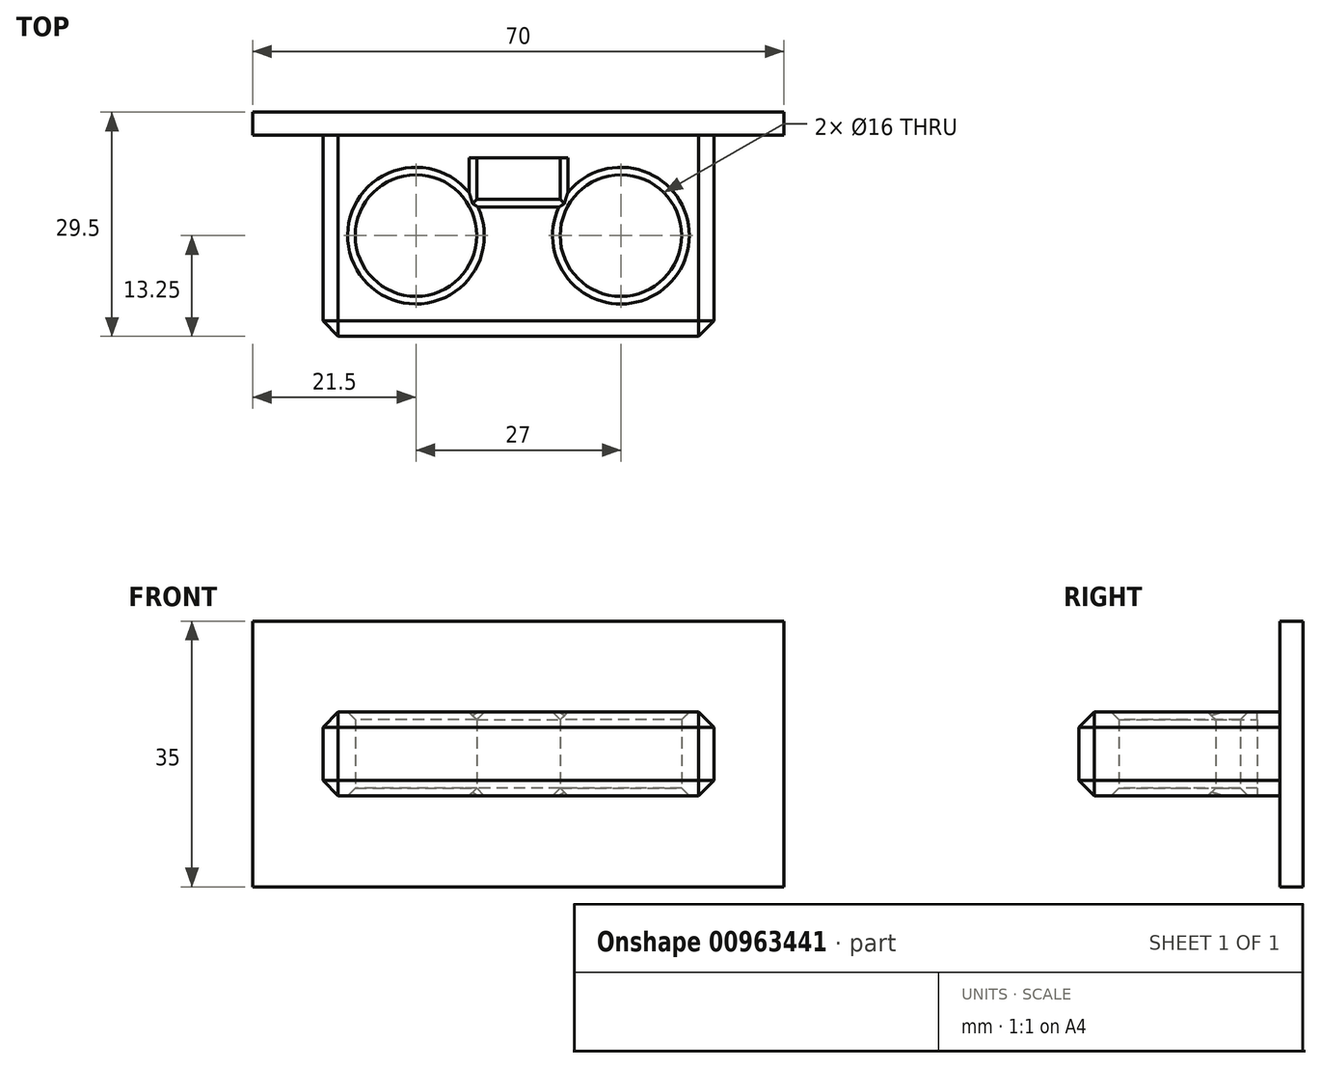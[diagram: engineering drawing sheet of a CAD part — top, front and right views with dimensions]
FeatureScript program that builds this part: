
annotation { "Feature Type Name" : "Feature", "Feature Type Description" : "" }
export const myFeature = defineFeature(function(context is Context, id is Id, definition is map)
    precondition{}
    {
        {
            var Q0;
            Q0=qCreatedBy(makeId("Top.planeOp"),FACE);
            var sketch = newSketch(context, id + "F0", { "sketchPlane" : qUnion([Q0])});
            skLineSegment(sketch, "E0.bottom", {"start": v(22.75, 10.25) * mm, "end": v(-22.75, 10.25) * mm});
            skLineSegment(sketch, "E0.top", {"start": v(22.75, -10.25) * mm, "end": v(-22.75, -10.25) * mm});
            skLineSegment(sketch, "E0.left", {"start": v(22.75, 10.25) * mm, "end": v(22.75, -10.25) * mm});
            skLineSegment(sketch, "E0.right", {"start": v(-22.75, 10.25) * mm, "end": v(-22.75, -10.25) * mm});
            skPoint(sketch, "E0.middle", {"position": v(0, 0) * mm});
            skLineSegment(sketch, "E1.bottom", {"start": v(13.5, 0) * mm, "end": v(-13.5, 0) * mm});
            skLineSegment(sketch, "E1.top", {"start": v(13.5, 0) * mm, "end": v(-13.5, 0) * mm});
            skLineSegment(sketch, "E1.left", {"start": v(13.5, 0) * mm, "end": v(13.5, 0) * mm});
            skLineSegment(sketch, "E1.right", {"start": v(-13.5, 0) * mm, "end": v(-13.5, 0) * mm});
            skCircle(sketch, "E2", {"center": v(-13.5, 0) * mm, "radius": 8 * mm});
            skCircle(sketch, "E3", {"center": v(13.5, 0) * mm, "radius": 8 * mm});
            skLineSegment(sketch, "E4.bottom", {"start": v(5.5, 10.25) * mm, "end": v(-5.5, 10.25) * mm});
            skLineSegment(sketch, "E4.top", {"start": v(5.5, 4.75) * mm, "end": v(-5.5, 4.75) * mm});
            skLineSegment(sketch, "E4.left", {"start": v(5.5, 10.25) * mm, "end": v(5.5, 4.75) * mm});
            skLineSegment(sketch, "E4.right", {"start": v(-5.5, 10.25) * mm, "end": v(-5.5, 4.75) * mm});
            skPoint(sketch, "E4.middle", {"position": v(0, 7.5) * mm});
            skLineSegment(sketch, "E5.0", {"start": v(25.75, 13.25) * mm, "end": v(-25.75, 13.25) * mm});
            skLineSegment(sketch, "E5.1", {"start": v(25.75, 13.25) * mm, "end": v(25.75, -13.25) * mm});
            skLineSegment(sketch, "E5.2", {"start": v(25.75, -13.25) * mm, "end": v(-25.75, -13.25) * mm});
            skLineSegment(sketch, "E5.3", {"start": v(-25.75, 13.25) * mm, "end": v(-25.75, -13.25) * mm});
            skSolve(sketch);
        }
        {
            var Q0;
            Q0=makeQuery(id+"F0.imprint","IMPRINT",FACE,{"disambiguationData":[TD([[makeQuery(id+"F0.imprint","IMPRINT",EDGE,{"derivedFrom":sQuery(id+"F0.wireOp",EDGE,"E0.top")}),1.0]])]});
            var Q1;
            Q1=makeQuery(id+"F0.imprint","IMPRINT",FACE,{"disambiguationData":[TD([[makeQuery(id+"F0.imprint","IMPRINT",EDGE,{"derivedFrom":sQuery(id+"F0.wireOp",EDGE,"E0.top")}),-1.0]])]});
            extrude(context, id + "F1", {"entities" : qUnion([Q0, Q1]), "depth" : 11 * mm, "offsetDistance" : 25 * mm});
        }
        {
            var Q0;
            Q0=makeQuery(id+"F1.opExtrude","SWEPT_FACE",FACE,{"disambiguationData":[OSD([sQuery(id+"F0.wireOp",EDGE,"E5.0")])]});
            var sketch = newSketch(context, id + "F2", { "sketchPlane" : qUnion([Q0])});
            skLineSegment(sketch, "E6", {"start": v(0, 0) * mm, "end": v(0, 11) * mm});
            skPoint(sketch, "E7", {"position": v(0, 5.5) * mm});
            skLineSegment(sketch, "E8.bottom", {"start": v(35, 23) * mm, "end": v(-35, 23) * mm});
            skLineSegment(sketch, "E8.top", {"start": v(35, -12) * mm, "end": v(-35, -12) * mm});
            skLineSegment(sketch, "E8.left", {"start": v(35, 23) * mm, "end": v(35, -12) * mm});
            skLineSegment(sketch, "E8.right", {"start": v(-35, 23) * mm, "end": v(-35, -12) * mm});
            skSolve(sketch);
        }
        {
            var Q0;
            Q0=makeQuery(id+"F2.imprint","IMPRINT",FACE,{"disambiguationData":[TD([[makeQuery(id+"F2.imprint","IMPRINT",EDGE,{"derivedFrom":sQuery(id+"F2.wireOp",EDGE,"E8.bottom")}),1.0]])]});
            var Q1;
            {var subQ0=sQuery(id+"F2.wireOp",EDGE,"E6");Q1=makeQuery(id+"F2.imprint","IMPRINT",FACE,{"disambiguationData":[TD([[makeQuery(id+"F2.imprint","IMPRINT",EDGE,{"derivedFrom":subQ0}),1.0]])]});}
            var Q2;
            {var subQ0=sQuery(id+"F2.wireOp",EDGE,"E6");Q2=makeQuery(id+"F2.imprint","IMPRINT",FACE,{"disambiguationData":[TD([[makeQuery(id+"F2.imprint","IMPRINT",EDGE,{"derivedFrom":subQ0}),-1.0]])]});}
            extrude(context, id + "F3", {"entities" : qUnion([Q0, Q1, Q2]), "operationType" : NewBodyOperationType.ADD, "depth" : 3 * mm, "offsetDistance" : 25 * mm});
        }
        {
            var Q0;
            Q0=makeQuery(id+"F1.opExtrude","SWEPT_EDGE",EDGE,{"disambiguationData":[OSD([sQuery(id+"F0.wireOp",EDGE,"E5.2"),sQuery(id+"F0.wireOp",EDGE,"E5.3")])]});
            var Q1;
            Q1=makeQuery(id+"F1.opExtrude","SWEPT_EDGE",EDGE,{"disambiguationData":[OSD([sQuery(id+"F0.wireOp",EDGE,"E5.1"),sQuery(id+"F0.wireOp",EDGE,"E5.2")])]});
            var Q2;
            Q2=makeQuery(id+"F1.opExtrude","CAP_EDGE",EDGE,{"disambiguationData":[OSD([sQuery(id+"F0.wireOp",EDGE,"E5.2")])],"isStart":false});
            var Q3;
            Q3=makeQuery(id+"F1.opExtrude","CAP_EDGE",EDGE,{"disambiguationData":[OSD([sQuery(id+"F0.wireOp",EDGE,"E5.1")])],"isStart":false});
            var Q4;
            Q4=makeQuery(id+"F1.opExtrude","CAP_EDGE",EDGE,{"disambiguationData":[OSD([sQuery(id+"F0.wireOp",EDGE,"E5.3")])],"isStart":false});
            var Q5;
            Q5=makeQuery(id+"F1.opExtrude","CAP_EDGE",EDGE,{"disambiguationData":[OSD([sQuery(id+"F0.wireOp",EDGE,"E5.1")])],"isStart":true});
            var Q6;
            Q6=makeQuery(id+"F1.opExtrude","CAP_EDGE",EDGE,{"disambiguationData":[OSD([sQuery(id+"F0.wireOp",EDGE,"E5.3")])],"isStart":true});
            var Q7;
            Q7=makeQuery(id+"F1.opExtrude","CAP_EDGE",EDGE,{"disambiguationData":[OSD([sQuery(id+"F0.wireOp",EDGE,"E5.2")])],"isStart":true});
            chamfer(context, id + "F4", {"entities" : qUnion([Q0, Q1, Q2, Q3, Q4, Q5, Q6, Q7]), "width" : 2 * mm, "tangentPropagation" : true});
        }
        {
            var Q0;
            Q0=makeQuery(id+"F1.opExtrude","CAP_EDGE",EDGE,{"disambiguationData":[OSD([sQuery(id+"F0.wireOp",EDGE,"E2")])],"isStart":true});
            var Q1;
            Q1=makeQuery(id+"F1.opExtrude","CAP_EDGE",EDGE,{"disambiguationData":[OSD([sQuery(id+"F0.wireOp",EDGE,"E3")])],"isStart":true});
            var Q2;
            Q2=makeQuery(id+"F1.opExtrude","CAP_EDGE",EDGE,{"disambiguationData":[OSD([sQuery(id+"F0.wireOp",EDGE,"E4.top")])],"isStart":true});
            var Q3;
            Q3=makeQuery(id+"F1.opExtrude","CAP_EDGE",EDGE,{"disambiguationData":[OSD([sQuery(id+"F0.wireOp",EDGE,"E4.left")])],"isStart":true});
            var Q4;
            Q4=makeQuery(id+"F1.opExtrude","CAP_EDGE",EDGE,{"disambiguationData":[OSD([sQuery(id+"F0.wireOp",EDGE,"E4.bottom")])],"isStart":true});
            var Q5;
            Q5=makeQuery(id+"F1.opExtrude","CAP_EDGE",EDGE,{"disambiguationData":[OSD([sQuery(id+"F0.wireOp",EDGE,"E4.right")])],"isStart":true});
            var Q6;
            Q6=makeQuery(id+"F1.opExtrude","CAP_EDGE",EDGE,{"disambiguationData":[OSD([sQuery(id+"F0.wireOp",EDGE,"E2")])],"isStart":false});
            var Q7;
            Q7=makeQuery(id+"F1.opExtrude","CAP_EDGE",EDGE,{"disambiguationData":[OSD([sQuery(id+"F0.wireOp",EDGE,"E3")])],"isStart":false});
            var Q8;
            Q8=makeQuery(id+"F1.opExtrude","CAP_EDGE",EDGE,{"disambiguationData":[OSD([sQuery(id+"F0.wireOp",EDGE,"E4.top")])],"isStart":false});
            var Q9;
            Q9=makeQuery(id+"F1.opExtrude","CAP_EDGE",EDGE,{"disambiguationData":[OSD([sQuery(id+"F0.wireOp",EDGE,"E4.right")])],"isStart":false});
            var Q10;
            Q10=makeQuery(id+"F1.opExtrude","CAP_EDGE",EDGE,{"disambiguationData":[OSD([sQuery(id+"F0.wireOp",EDGE,"E4.bottom")])],"isStart":false});
            var Q11;
            Q11=makeQuery(id+"F1.opExtrude","CAP_EDGE",EDGE,{"disambiguationData":[OSD([sQuery(id+"F0.wireOp",EDGE,"E4.left")])],"isStart":false});
            chamfer(context, id + "F5", {"entities" : qUnion([Q0, Q1, Q2, Q3, Q4, Q5, Q6, Q7, Q8, Q9, Q10, Q11]), "width" : 1 * mm, "tangentPropagation" : true});
        }
    });
